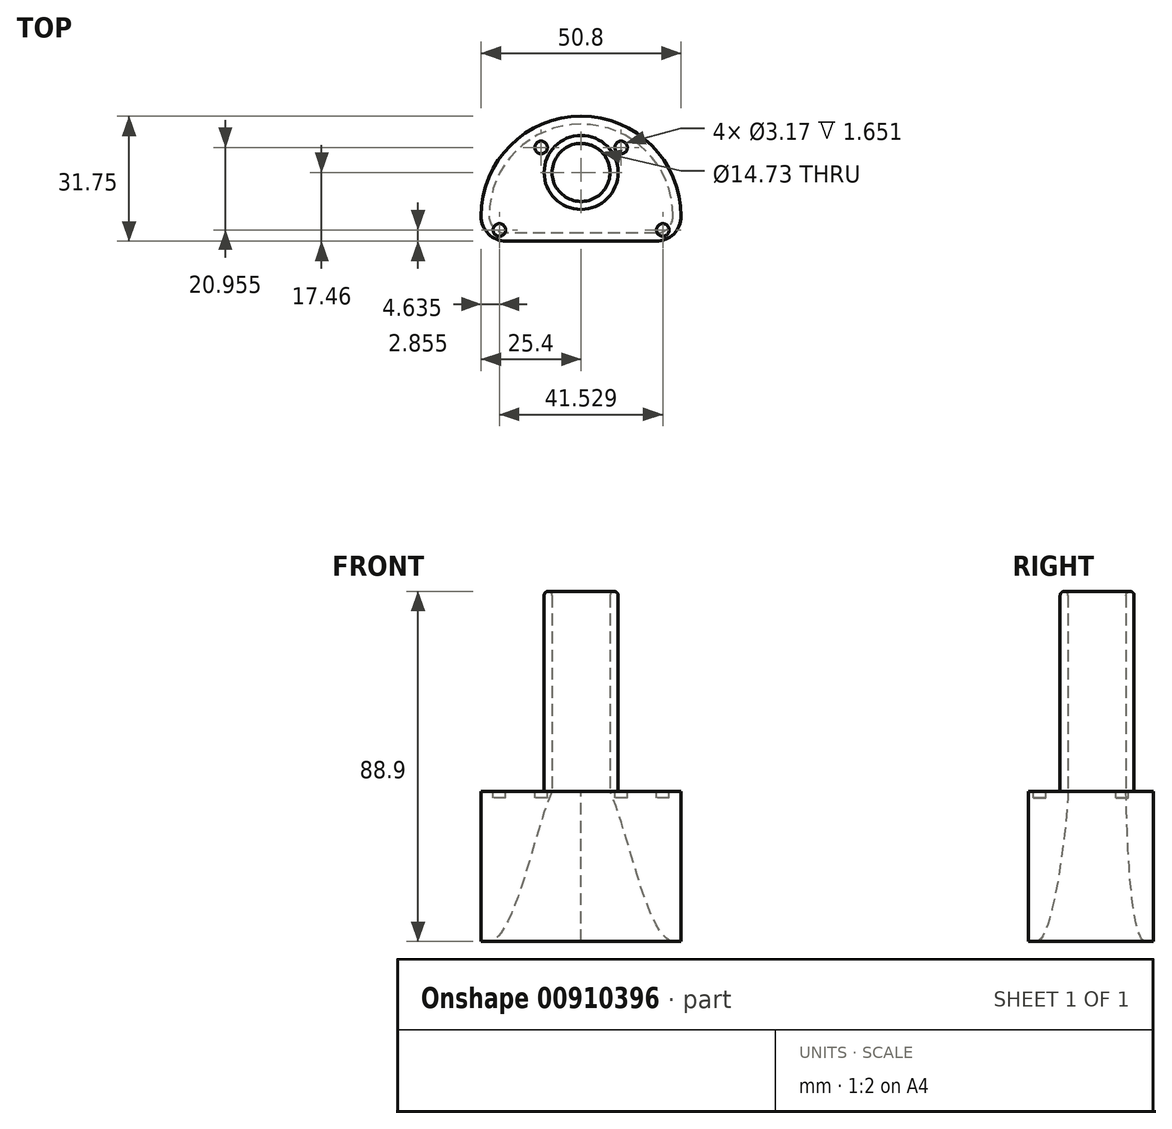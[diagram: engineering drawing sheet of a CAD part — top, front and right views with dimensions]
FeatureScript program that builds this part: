
annotation { "Feature Type Name" : "Feature", "Feature Type Description" : "" }
export const myFeature = defineFeature(function(context is Context, id is Id, definition is map)
    precondition{}
    {
        {
            var Q0;
            Q0=qCreatedBy(makeId("Top.planeOp"),FACE);
            var sketch = newSketch(context, id + "F0", { "sketchPlane" : qUnion([Q0])});
            skLineSegment(sketch, "E0.bottom", {"start": v(25.4, 17.46) * mm, "end": v(-25.4, 17.46) * mm, "construction": true});
            skLineSegment(sketch, "E0.top", {"start": v(25.4, -17.46) * mm, "end": v(-25.4, -17.46) * mm});
            skLineSegment(sketch, "E0.left", {"start": v(25.4, 17.46) * mm, "end": v(25.4, -17.46) * mm, "construction": true});
            skLineSegment(sketch, "E0.right", {"start": v(-25.4, 17.46) * mm, "end": v(-25.4, -17.46) * mm, "construction": true});
            skPoint(sketch, "E0.middle", {"position": v(0, 0) * mm});
            skCircle(sketch, "E1", {"center": v(0, 0) * mm, "radius": 9.53 * mm, "construction": true});
            skLineSegment(sketch, "E2.bottom", {"start": v(13.97, 15.43) * mm, "end": v(-13.97, 15.43) * mm, "construction": true});
            skLineSegment(sketch, "E2.top", {"start": v(13.97, -15.43) * mm, "end": v(-13.97, -15.43) * mm, "construction": true});
            skLineSegment(sketch, "E2.left", {"start": v(19.05, 10.35) * mm, "end": v(19.05, -10.35) * mm, "construction": true});
            skLineSegment(sketch, "E2.right", {"start": v(-19.05, 10.35) * mm, "end": v(-19.05, -10.35) * mm, "construction": true});
            skPoint(sketch, "E3.visualSharp", {"position": v(-19.05, 15.43) * mm});
            skArc(sketch, "E3.filletArc", {"start": v(-13.97, 15.43) * mm, "mid": v(-17.56, 13.94) * mm, "end": v(-19.05, 10.35) * mm, "construction": true});
            skPoint(sketch, "E4.visualSharp", {"position": v(-19.05, -15.43) * mm});
            skArc(sketch, "E4.filletArc", {"start": v(-19.05, -10.35) * mm, "mid": v(-17.56, -13.94) * mm, "end": v(-13.97, -15.43) * mm, "construction": true});
            skPoint(sketch, "E5.visualSharp", {"position": v(19.05, -15.43) * mm});
            skArc(sketch, "E5.filletArc", {"start": v(13.97, -15.43) * mm, "mid": v(17.56, -13.94) * mm, "end": v(19.05, -10.35) * mm, "construction": true});
            skPoint(sketch, "E6.visualSharp", {"position": v(19.05, 15.43) * mm});
            skArc(sketch, "E6.filletArc", {"start": v(19.05, 10.35) * mm, "mid": v(17.56, 13.94) * mm, "end": v(13.97, 15.43) * mm, "construction": true});
            skLineSegment(sketch, "E7", {"start": v(-25.4, -17.46) * mm, "end": v(-25.4, -11.11) * mm});
            skLineSegment(sketch, "E8", {"start": v(25.4, -17.46) * mm, "end": v(25.4, -11.11) * mm});
            skArc(sketch, "E9", {"start": v(25.4, -11.11) * mm, "mid": v(0, 14.29) * mm, "end": v(-25.4, -11.11) * mm});
            skSolve(sketch);
        }
        {
            var Q0;
            Q0 = qSketchRegion(id + "F0", true);
            extrude(context, id + "F1", {"entities" : qUnion([Q0]), "depth" : 38.1 * mm, "offsetDistance" : 25.4 * mm});
        }
        {
            var Q0;
            Q0=makeQuery(id+"F1.opExtrude","CAP_FACE",FACE,{"disambiguationData":[OSD([sQuery(id+"F0.wireOp",EDGE,"E0.bottom"),sQuery(id+"F0.wireOp",EDGE,"E0.top"),sQuery(id+"F0.wireOp",EDGE,"E0.left"),sQuery(id+"F0.wireOp",EDGE,"E0.right")])],"isStart":false});
            var sketch = newSketch(context, id + "F2", { "sketchPlane" : qUnion([Q0])});
            skCircle(sketch, "E10", {"center": v(0, 0) * mm, "radius": 9.4 * mm});
            skCircle(sketch, "E11", {"center": v(0, 0) * mm, "radius": 7.37 * mm});
            skSolve(sketch);
        }
        {
            var Q0;
            Q0 = qSketchRegion(id + "F2", true);
            extrude(context, id + "F3", {"entities" : qUnion([Q0]), "operationType" : NewBodyOperationType.ADD, "depth" : 50.8 * mm, "offsetDistance" : 25.4 * mm});
        }
        {
            var Q0;
            Q0=makeQuery(id+"F3.opExtrude","CAP_EDGE",EDGE,{"disambiguationData":[OSD([sQuery(id+"F2.wireOp",EDGE,"E11")])],"isStart":false});
            var Q1;
            Q1=makeQuery(id+"F3.opExtrude","CAP_EDGE",EDGE,{"disambiguationData":[OSD([sQuery(id+"F2.wireOp",EDGE,"E10")])],"isStart":false});
            fillet(context, id + "F4", {"entities" : qUnion([Q0, Q1]), "radius" : 1.02 * mm, "tangentPropagation" : true, "allowEdgeOverflow" : false});
        }
        {
            var Q0;
            Q0=makeQuery(id+"F1.opExtrude","SWEPT_EDGE",EDGE,{"disambiguationData":[OSD([sQuery(id+"F0.wireOp",EDGE,"E0.top"),sQuery(id+"F0.wireOp",EDGE,"E0.right")])]});
            var Q1;
            Q1=makeQuery(id+"F1.opExtrude","SWEPT_EDGE",EDGE,{"disambiguationData":[OSD([sQuery(id+"F0.wireOp",EDGE,"E0.bottom"),sQuery(id+"F0.wireOp",EDGE,"E0.right")])]});
            var Q2;
            Q2=makeQuery(id+"F1.opExtrude","SWEPT_EDGE",EDGE,{"disambiguationData":[OSD([sQuery(id+"F0.wireOp",EDGE,"E0.bottom"),sQuery(id+"F0.wireOp",EDGE,"E0.left")])]});
            var Q3;
            Q3=makeQuery(id+"F1.opExtrude","SWEPT_EDGE",EDGE,{"disambiguationData":[OSD([sQuery(id+"F0.wireOp",EDGE,"E0.top"),sQuery(id+"F0.wireOp",EDGE,"E0.left")])]});
            var Q4;
            Q4=makeQuery(id+"F1.opExtrude","SWEPT_EDGE",EDGE,{"disambiguationData":[OSD([sQuery(id+"F0.wireOp",EDGE,"E8"),sQuery(id+"F0.wireOp",EDGE,"E9")])]});
            var Q5;
            Q5=makeQuery(id+"F1.opExtrude","SWEPT_EDGE",EDGE,{"disambiguationData":[OSD([sQuery(id+"F0.wireOp",EDGE,"E7"),sQuery(id+"F0.wireOp",EDGE,"E9")])]});
            fillet(context, id + "F5", {"entities" : qUnion([Q0, Q1, Q2, Q3, Q4, Q5]), "radius" : 6.35 * mm, "tangentPropagation" : true, "allowEdgeOverflow" : false});
        }
        {
            var Q0;
            Q0=makeQuery(id+"F1.opExtrude","CAP_FACE",FACE,{"disambiguationData":[OSD([sQuery(id+"F0.wireOp",EDGE,"E0.bottom"),sQuery(id+"F0.wireOp",EDGE,"E0.top"),sQuery(id+"F0.wireOp",EDGE,"E0.left"),sQuery(id+"F0.wireOp",EDGE,"E0.right")])],"isStart":true});
            var sketch = newSketch(context, id + "F6", { "sketchPlane" : qUnion([Q0])});
            skLineSegment(sketch, "E12.0", {"start": v(19.05, 15.43) * mm, "end": v(-19.05, 15.43) * mm});
            skArc(sketch, "E12.1", {"start": v(23.37, 11.11) * mm, "mid": v(22.1, 14.17) * mm, "end": v(19.05, 15.43) * mm});
            skArc(sketch, "E12.2", {"start": v(-19.05, 15.43) * mm, "mid": v(-22.1, 14.17) * mm, "end": v(-23.37, 11.11) * mm});
            skArc(sketch, "E12.6", {"start": v(23.37, 11.11) * mm, "mid": v(0, -12.26) * mm, "end": v(-23.37, 11.11) * mm});
            skSolve(sketch);
        }
        {
            var Q0;
            Q0=qCreatedBy(makeId("Right.planeOp"),FACE);
            var sketch = newSketch(context, id + "F7", { "sketchPlane" : qUnion([Q0])});
            skFitSpline(sketch, "E13", {"points": [v(12.26, 0) * mm, v(7.37, 38.1) * mm], "startDerivative": vector(-9.14, 0) * mm, "endDerivative": vector(-0.86, 58.04) * mm});
            skLineSegment(sketch, "E14.0", {"start": v(-11.11, 0) * mm, "end": v(12.26, 0) * mm, "construction": true});
            skLineSegment(sketch, "E14.1", {"start": v(-7.37, 38.1) * mm, "end": v(7.37, 38.1) * mm, "construction": true});
            skFitSpline(sketch, "E15", {"points": [v(-7.37, 38.1) * mm, v(-15.43, 0) * mm], "startDerivative": vector(-0.01, -15.85) * mm, "endDerivative": vector(-13.53, 0) * mm});
            skSolve(sketch);
        }
        {
            var Q1;
            Q1 = qSketchRegion(id + "F6", true);
            var Q2;
            Q2=makeQuery(id+"F3.boolean.opBoolean","SPLIT",FACE,{"disambiguationData":[TD([makeQuery(id+"F3.opExtrude","SWEPT_FACE",FACE,{"disambiguationData":[OSD([sQuery(id+"F2.wireOp",EDGE,"E11")])]})])],"derivedFrom":makeQuery(id+"F1.opExtrude","CAP_FACE",FACE,{"disambiguationData":[OSD([sQuery(id+"F0.wireOp",EDGE,"E0.bottom"),sQuery(id+"F0.wireOp",EDGE,"E0.top"),sQuery(id+"F0.wireOp",EDGE,"E0.left"),sQuery(id+"F0.wireOp",EDGE,"E0.right")])],"isStart":false})});
            var Q3;
            Q3=sQuery(id+"F7.wireOp",EDGE,"E13");
            var Q4;
            Q4=sQuery(id+"F7.wireOp",EDGE,"E15");
            loft(context, id + "F8", {"operationType" : NewBodyOperationType.REMOVE, "addGuides" : true, "sheetProfilesArray" : [{ "sheetProfileEntities" : qUnion([Q1]) }, { "sheetProfileEntities" : qUnion([Q2]) }], "guidesArray" : [{ "guideEntities" : qUnion([Q3]), "guideDerivativeType" : LoftGuideDerivativeType.DEFAULT, "guideDerivativeMagnitude" : 1 }, { "guideEntities" : qUnion([Q4]), "guideDerivativeType" : LoftGuideDerivativeType.DEFAULT, "guideDerivativeMagnitude" : 1 }]});
        }
        {
            var Q0;
            Q0=makeQuery(id+"F2.imprint","IMPRINT",FACE,{"disambiguationData":[TD([[makeQuery(id+"F2.imprint","IMPRINT",EDGE,{"derivedFrom":sQuery(id+"F2.wireOp",EDGE,"E10")}),-1.0]])]});
            var sketch = newSketch(context, id + "F9", { "sketchPlane" : qUnion([Q0])});
            skCircle(sketch, "E16", {"center": v(20.76, -14.6) * mm, "radius": 1.59 * mm});
            skCircle(sketch, "E17", {"center": v(-20.76, -14.6) * mm, "radius": 1.59 * mm});
            skCircle(sketch, "E18", {"center": v(10.16, 6.35) * mm, "radius": 1.59 * mm});
            skCircle(sketch, "E19", {"center": v(-10.16, 6.35) * mm, "radius": 1.59 * mm});
            skLineSegment(sketch, "E20", {"start": v(20.76, -14.6) * mm, "end": v(-20.76, -14.6) * mm, "construction": true});
            skLineSegment(sketch, "E21", {"start": v(0, 6.35) * mm, "end": v(0, -14.6) * mm, "construction": true});
            skLineSegment(sketch, "E22", {"start": v(10.16, 6.35) * mm, "end": v(-10.16, 6.35) * mm, "construction": true});
            skSolve(sketch);
        }
        {
            var Q0;
            Q0 = qSketchRegion(id + "F9", true);
            extrude(context, id + "F10", {"entities" : qUnion([Q0]), "operationType" : NewBodyOperationType.REMOVE, "oppositeDirection" : true, "depth" : 1.65 * mm, "offsetDistance" : 25.4 * mm});
        }
    });
